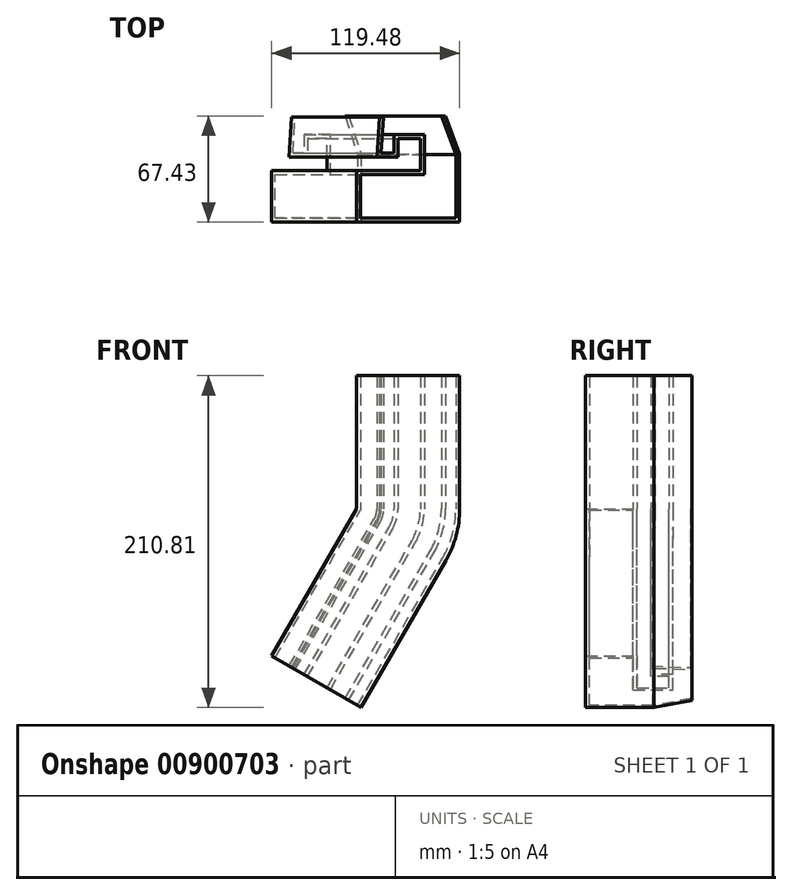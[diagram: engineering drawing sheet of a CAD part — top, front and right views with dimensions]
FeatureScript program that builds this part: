
annotation { "Feature Type Name" : "Feature", "Feature Type Description" : "" }
export const myFeature = defineFeature(function(context is Context, id is Id, definition is map)
    precondition{}
    {
        {
            var Q0;
            Q0=qCreatedBy(makeId("Top.planeOp"),FACE);
            var sketch = newSketch(context, id + "F0", { "sketchPlane" : qUnion([Q0])});
            skLineSegment(sketch, "E0", {"start": v(0, 0) * mm, "end": v(40.54, 0) * mm});
            skLineSegment(sketch, "E1", {"start": v(40.54, 0) * mm, "end": v(40.54, 20.4) * mm});
            skLineSegment(sketch, "E2", {"start": v(40.54, 20.4) * mm, "end": v(26.27, 20.4) * mm});
            skLineSegment(sketch, "E3", {"start": v(26.27, 20.4) * mm, "end": v(26.27, 8.86) * mm});
            skLineSegment(sketch, "E4", {"start": v(26.27, 8.86) * mm, "end": v(12.94, 8.86) * mm});
            skLineSegment(sketch, "E5", {"start": v(12.94, 8.86) * mm, "end": v(14.74, 34.1) * mm});
            skLineSegment(sketch, "E6", {"start": v(14.74, 34.1) * mm, "end": v(56.54, 34.82) * mm});
            skLineSegment(sketch, "E7", {"start": v(56.54, 34.82) * mm, "end": v(65.55, 10.66) * mm});
            skLineSegment(sketch, "E8", {"start": v(65.55, 10.66) * mm, "end": v(65.55, -32.6) * mm});
            skLineSegment(sketch, "E9", {"start": v(65.55, -32.6) * mm, "end": v(0, -32.6) * mm});
            skLineSegment(sketch, "E10", {"start": v(0, -32.6) * mm, "end": v(0, 0) * mm});
            skLineSegment(sketch, "E11", {"start": v(0, 0) * mm, "end": v(0, 67.17) * mm, "construction": true});
            skSolve(sketch);
        }
        {
            var Q0;
            Q0=makeQuery(id+"F0.imprint","IMPRINT",FACE,{"disambiguationData":[TD([[makeQuery(id+"F0.imprint","IMPRINT",EDGE,{"derivedFrom":sQuery(id+"F0.wireOp",EDGE,"E0")}),-1.0]])]});
            var Q1;
            Q1=sQuery(id+"F0.wireOp",EDGE,"E11");
            revolve(context, id + "F1", {"surfaceOperationType" : NewSurfaceOperationType.NEW, "entities" : qUnion([Q0]), "axis" : qUnion([Q1]), "revolveType" : RevolveType.ONE_DIRECTION, "angle" : 30 * degree});
        }
        {
            var Q0;
            Q0=makeQuery(id+"F1.opRevolve","CAP_FACE",FACE,{"disambiguationData":[OSD([sQuery(id+"F0.wireOp",EDGE,"E0"),sQuery(id+"F0.wireOp",EDGE,"E1"),sQuery(id+"F0.wireOp",EDGE,"E2"),sQuery(id+"F0.wireOp",EDGE,"E3"),sQuery(id+"F0.wireOp",EDGE,"E4"),sQuery(id+"F0.wireOp",EDGE,"E5"),sQuery(id+"F0.wireOp",EDGE,"E6"),sQuery(id+"F0.wireOp",EDGE,"E7"),sQuery(id+"F0.wireOp",EDGE,"E8"),sQuery(id+"F0.wireOp",EDGE,"E9"),sQuery(id+"F0.wireOp",EDGE,"E10")])],"isStart":true});
            extrude(context, id + "F2", {"entities" : qUnion([Q0]), "operationType" : NewBodyOperationType.ADD, "depth" : 84.63 * mm, "offsetDistance" : 25 * mm});
        }
        {
            var Q0;
            Q0=makeQuery(id+"F1.opRevolve","CAP_FACE",FACE,{"disambiguationData":[OSD([sQuery(id+"F0.wireOp",EDGE,"E0"),sQuery(id+"F0.wireOp",EDGE,"E1"),sQuery(id+"F0.wireOp",EDGE,"E2"),sQuery(id+"F0.wireOp",EDGE,"E3"),sQuery(id+"F0.wireOp",EDGE,"E4"),sQuery(id+"F0.wireOp",EDGE,"E5"),sQuery(id+"F0.wireOp",EDGE,"E6"),sQuery(id+"F0.wireOp",EDGE,"E7"),sQuery(id+"F0.wireOp",EDGE,"E8"),sQuery(id+"F0.wireOp",EDGE,"E9"),sQuery(id+"F0.wireOp",EDGE,"E10")])],"isStart":false});
            extrude(context, id + "F3", {"entities" : qUnion([Q0]), "operationType" : NewBodyOperationType.ADD, "depth" : 107.86 * mm, "offsetDistance" : 25 * mm});
        }
        {
            var Q0;
            Q0=makeQuery(id+"F3.opExtrude","SWEPT_FACE",FACE,{"disambiguationData":[OSD([sQuery(id+"F0.wireOp",EDGE,"E6")])]});
            var Q1;
            Q1=makeQuery(id+"F1.opRevolve","SWEPT_FACE",FACE,{"disambiguationData":[OSD([sQuery(id+"F0.wireOp",EDGE,"E6")])]});
            var Q2;
            Q2=makeQuery(id+"F2.opExtrude","SWEPT_FACE",FACE,{"disambiguationData":[OSD([sQuery(id+"F0.wireOp",EDGE,"E6")])]});
            var Q3;
            Q3=makeQuery(id+"F2.opExtrude","CAP_FACE",FACE,{"disambiguationData":[OSD([sQuery(id+"F0.wireOp",EDGE,"E0"),sQuery(id+"F0.wireOp",EDGE,"E1"),sQuery(id+"F0.wireOp",EDGE,"E2"),sQuery(id+"F0.wireOp",EDGE,"E3"),sQuery(id+"F0.wireOp",EDGE,"E4"),sQuery(id+"F0.wireOp",EDGE,"E5"),sQuery(id+"F0.wireOp",EDGE,"E6"),sQuery(id+"F0.wireOp",EDGE,"E7"),sQuery(id+"F0.wireOp",EDGE,"E8"),sQuery(id+"F0.wireOp",EDGE,"E9"),sQuery(id+"F0.wireOp",EDGE,"E10")])],"isStart":false});
            var Q4;
            Q4=makeQuery(id+"F3.opExtrude","CAP_FACE",FACE,{"disambiguationData":[OSD([sQuery(id+"F0.wireOp",EDGE,"E0"),sQuery(id+"F0.wireOp",EDGE,"E1"),sQuery(id+"F0.wireOp",EDGE,"E2"),sQuery(id+"F0.wireOp",EDGE,"E3"),sQuery(id+"F0.wireOp",EDGE,"E4"),sQuery(id+"F0.wireOp",EDGE,"E5"),sQuery(id+"F0.wireOp",EDGE,"E6"),sQuery(id+"F0.wireOp",EDGE,"E7"),sQuery(id+"F0.wireOp",EDGE,"E8"),sQuery(id+"F0.wireOp",EDGE,"E9"),sQuery(id+"F0.wireOp",EDGE,"E10")])],"isStart":false});
            shell(context, id + "F4", {"entities" : qUnion([Q0, Q1, Q2, Q3, Q4]), "thickness" : 2.5 * mm});
        }
    });
